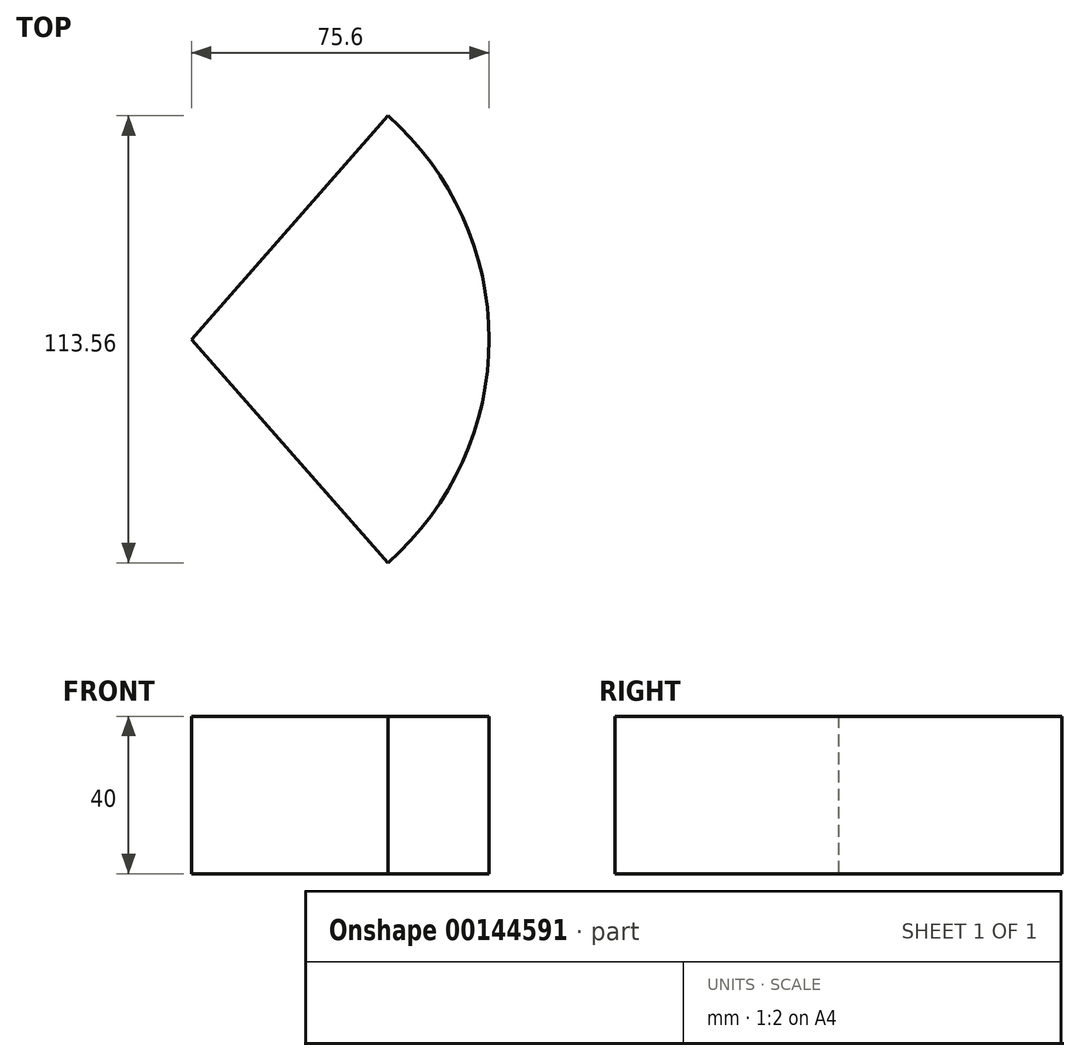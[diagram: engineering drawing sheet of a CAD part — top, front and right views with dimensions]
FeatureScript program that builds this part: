
annotation { "Feature Type Name" : "Feature", "Feature Type Description" : "" }
export const myFeature = defineFeature(function(context is Context, id is Id, definition is map)
    precondition{}
    {
        {
            var Q0;
            Q0=qCreatedBy(makeId("Front.planeOp"),FACE);
            var sketch = newSketch(context, id + "F0", { "sketchPlane" : qUnion([Q0])});
            skLineSegment(sketch, "E0.bottom", {"start": v(37.8, 20) * mm, "end": v(-37.8, 20) * mm});
            skLineSegment(sketch, "E0.top", {"start": v(37.8, -20) * mm, "end": v(-37.8, -20) * mm});
            skLineSegment(sketch, "E0.left", {"start": v(37.8, 20) * mm, "end": v(37.8, -20) * mm});
            skLineSegment(sketch, "E0.right", {"start": v(-37.8, 20) * mm, "end": v(-37.8, -20) * mm});
            skPoint(sketch, "E0.middle", {"position": v(0, 0) * mm});
            skSolve(sketch);
        }
        {
            var Q0;
            Q0 = qSketchRegion(id + "F0", true);
            var Q1;
            Q1=sQuery(id+"F0.wireOp",EDGE,"E0.right");
            revolve(context, id + "F1", {"entities" : qUnion([Q0]), "axis" : qUnion([Q1]), "revolveType" : RevolveType.SYMMETRIC, "angle" : 97.36 * degree});
        }
    });
